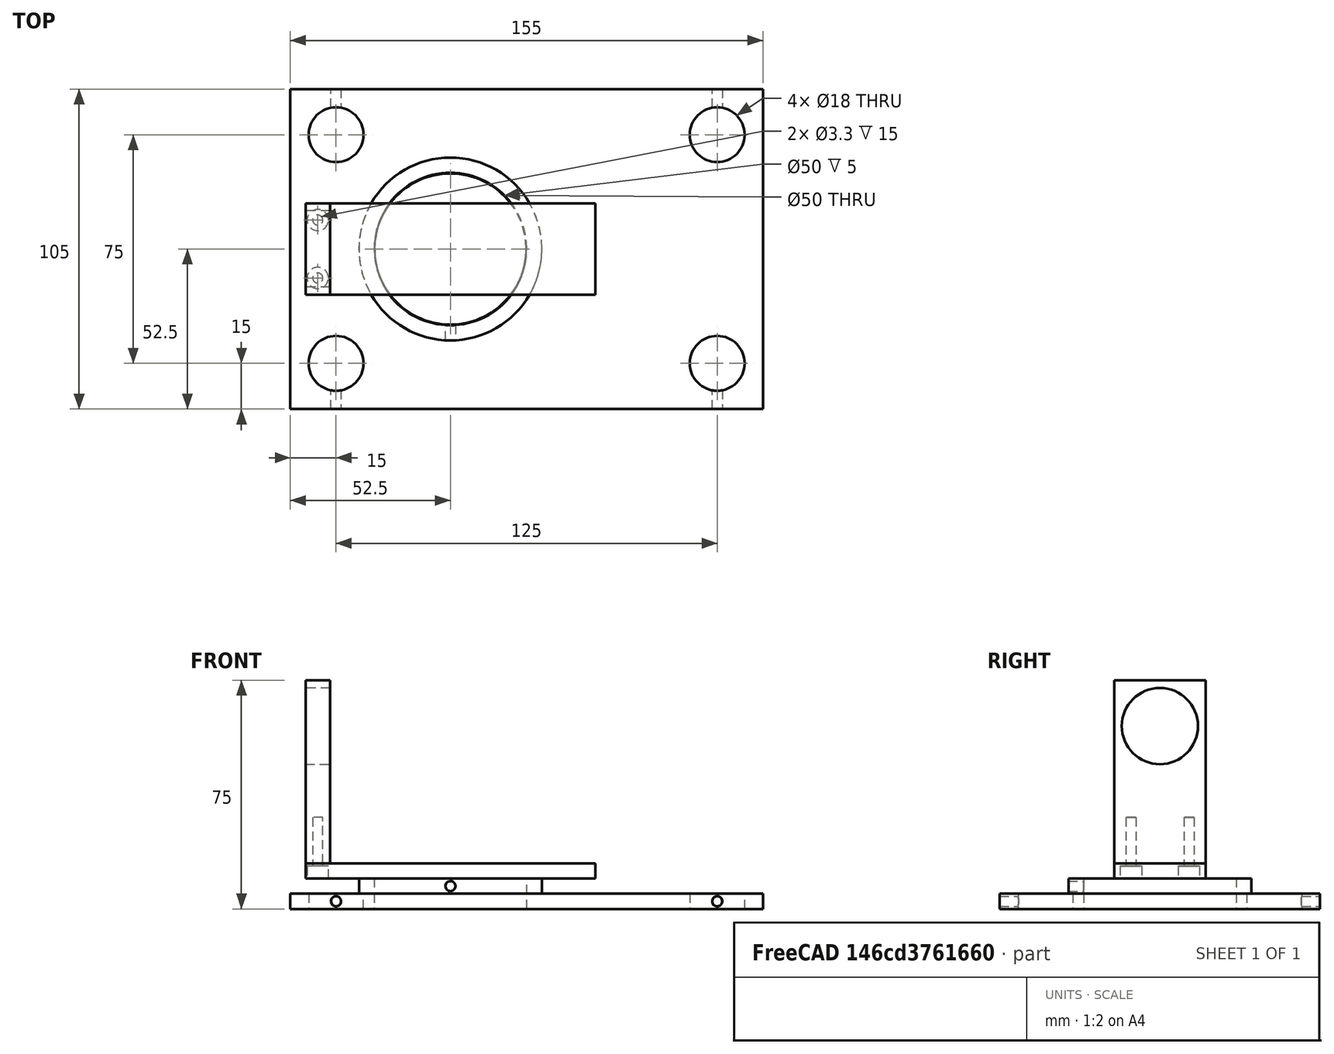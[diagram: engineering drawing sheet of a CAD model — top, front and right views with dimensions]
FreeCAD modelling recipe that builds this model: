
FCSTD DOCUMENT  (FreeCAD 0.21R33675 (Git))
Label: CameraObjectiveMount01
License: All rights reserved
LicenseURL: http://en.wikipedia.org/wiki/All_rights_reserved
objects: Part::Cylinder×20, Part::Cut×8, Part::Compound×4, Part::MultiFuse×4, Part::Box×3, Part::Feature×3
note: 42 computed .brp shape members not serialized (recipe doc carries the construction recipe); baked Part::Feature solids carry a one-line shape summary decoded from their .brp

FEATURE [Part::Box] Box  label="Würfel"
  AttacherType = Attacher::AttachEngine3D
  Height = 5
  Length = 155
  Placement = pos=(-5,-5,0) rot=(0,0,1;0rad)
  Width = 105
FEATURE [Part::Cylinder] Cylinder  label="Zylinder"
  Angle = 360
  AttacherType = Attacher::AttachEngine3D
  FirstAngle = 0
  Height = 100
  Placement = pos=(10,10,-10) rot=(0,0,1;0rad)
  Radius = 9
  SecondAngle = 0
FEATURE [Part::Cylinder] Cylinder001  label="Zylinder001"
  Angle = 360
  AttacherType = Attacher::AttachEngine3D
  FirstAngle = 0
  Height = 100
  Placement = pos=(135,85,-10) rot=(0,0,1;0rad)
  Radius = 9
  SecondAngle = 0
FEATURE [Part::Cylinder] Cylinder002  label="Zylinder002"
  Angle = 360
  AttacherType = Attacher::AttachEngine3D
  FirstAngle = 0
  Height = 100
  Placement = pos=(10,85,-10) rot=(0,0,1;0rad)
  Radius = 9
  SecondAngle = 0
FEATURE [Part::Cylinder] Cylinder003  label="Zylinder003"
  Angle = 360
  AttacherType = Attacher::AttachEngine3D
  FirstAngle = 0
  Height = 100
  Placement = pos=(135,10,-10) rot=(0,0,1;0rad)
  Radius = 9
  SecondAngle = 0
FEATURE [Part::Compound] Compound  label="Posts1"
  Links = -> [Cylinder,Cylinder001,Cylinder002,Cylinder003]
FEATURE [Part::Cut] Cut
  Base = -> Box
  Tool = -> Compound
FEATURE [Part::Cylinder] Cylinder004  label="Zylinder004"
  Angle = 360
  AttacherType = Attacher::AttachEngine3D
  FirstAngle = 0
  Height = 10
  Placement = pos=(10,5,2.5) rot=(1,0,0;1.5708rad)
  Radius = 1.65
  SecondAngle = 0
FEATURE [Part::Cylinder] Cylinder005  label="Zylinder005"
  Angle = 360
  AttacherType = Attacher::AttachEngine3D
  FirstAngle = 0
  Height = 10
  Placement = pos=(10,100,2.5) rot=(1,0,0;1.5708rad)
  Radius = 1.65
  SecondAngle = 0
FEATURE [Part::Cylinder] Cylinder006  label="Zylinder006"
  Angle = 360
  AttacherType = Attacher::AttachEngine3D
  FirstAngle = 0
  Height = 10
  Placement = pos=(135,5,2.5) rot=(1,0,0;1.5708rad)
  Radius = 1.65
  SecondAngle = 0
FEATURE [Part::Cylinder] Cylinder007  label="Zylinder007"
  Angle = 360
  AttacherType = Attacher::AttachEngine3D
  FirstAngle = 0
  Height = 10
  Placement = pos=(135,100,2.5) rot=(1,0,0;1.5708rad)
  Radius = 1.65
  SecondAngle = 0
FEATURE [Part::Compound] Compound001
  Links = -> [Cylinder007,Cylinder004,Cylinder005,Cylinder006]
FEATURE [Part::Cut] Cut001
  Base = -> Cut
  Tool = -> Compound001
FEATURE [Part::Cylinder] Cylinder008  label="Zylinder008"
  Angle = 360
  AttacherType = Attacher::AttachEngine3D
  FirstAngle = 0
  Height = 5
  Placement = pos=(47.5,47.5,5) rot=(0,0,1;0rad)
  Radius = 30
  SecondAngle = 0
FEATURE [Part::Cylinder] Cylinder009  label="Zylinder009"
  Angle = 360
  AttacherType = Attacher::AttachEngine3D
  FirstAngle = 0
  Height = 10
  Placement = pos=(47.5,47.5,0) rot=(0,0,1;0rad)
  Radius = 25
  SecondAngle = 0
FEATURE [Part::Cut] Cut002
  Base = -> Cylinder008
  Tool = -> Cylinder009
FEATURE [Part::Cylinder] Cylinder010  label="Zylinder010"
  Angle = 360
  AttacherType = Attacher::AttachEngine3D
  FirstAngle = 0
  Height = 10
  Placement = pos=(47.5,47.5,0) rot=(0,0,1;0rad)
  Radius = 24.8
  SecondAngle = 0
FEATURE [Part::Box] Box001  label="Würfel001"
  AttacherType = Attacher::AttachEngine3D
  Height = 5
  Length = 95
  Placement = pos=(0,32.5,10) rot=(0,0,1;0rad)
  Width = 30
FEATURE [Part::Box] Box002  label="Würfel002"
  AttacherType = Attacher::AttachEngine3D
  Height = 60
  Length = 8
  Placement = pos=(0,32.5,15) rot=(0,0,1;0rad)
  Width = 30
FEATURE [Part::Cylinder] Cylinder011  label="Zylinder011"
  Angle = 360
  AttacherType = Attacher::AttachEngine3D
  FirstAngle = 0
  Height = 10
  Placement = pos=(0,47.5,60) rot=(0,1,0;1.5708rad)
  Radius = 12.5
  SecondAngle = 0
FEATURE [Part::Cut] Cut003
  Base = -> Box002
  Tool = -> Cylinder011
FEATURE [Part::Cylinder] Cylinder012  label="Zylinder012"
  Angle = 360
  AttacherType = Attacher::AttachEngine3D
  FirstAngle = 0
  Height = 10
  Placement = pos=(47.5,47.5,0) rot=(0,0,1;0rad)
  Radius = 25
  SecondAngle = 0
FEATURE [Part::Cut] Cut004
  Base = -> Cut001
  Tool = -> Cylinder012
FEATURE [Part::Cylinder] Cylinder013  label="Zylinder013"
  Angle = 360
  AttacherType = Attacher::AttachEngine3D
  FirstAngle = 0
  Height = 10
  Placement = pos=(47.5,25,7.5) rot=(1,0,0;1.5708rad)
  Radius = 1.65
  SecondAngle = 0
FEATURE [Part::MultiFuse] Fusion
  Shapes = -> [Cut002,Cut004]
FEATURE [Part::Cut] Cut005  label="Plate"
  Base = -> Fusion
  Tool = -> Cylinder013
FEATURE [Part::MultiFuse] Fusion001
  Shapes = -> [Cylinder010,Box001]
FEATURE [Part::Cylinder] Cylinder014  label="Zylinder014"
  Angle = 360
  AttacherType = Attacher::AttachEngine3D
  FirstAngle = 0
  Height = 20
  Radius = 1.65
  SecondAngle = 0
FEATURE [Part::Cylinder] Cylinder015  label="Zylinder015"
  Angle = 360
  AttacherType = Attacher::AttachEngine3D
  FirstAngle = 0
  Height = 20
  Radius = 1.65
  SecondAngle = 0
FEATURE [Part::Cylinder] Cylinder016  label="Zylinder016"
  Angle = 360
  AttacherType = Attacher::AttachEngine3D
  FirstAngle = 0
  Height = 4
  Radius = 3.5
  SecondAngle = 0
FEATURE [Part::Cylinder] Cylinder017  label="Zylinder017"
  Angle = 360
  AttacherType = Attacher::AttachEngine3D
  FirstAngle = 0
  Height = 4
  Radius = 3.5
  SecondAngle = 0
FEATURE [Part::MultiFuse] Fusion002  label="Screw01"
  Placement = pos=(4,38,10) rot=(0,0,1;0rad)
  Shapes = -> [Cylinder014,Cylinder016]
FEATURE [Part::MultiFuse] Fusion003  label="Screw02"
  Placement = pos=(4,57,10) rot=(0,0,1;0rad)
  Shapes = -> [Cylinder015,Cylinder017]
FEATURE [Part::Compound] Compound002
  Links = -> [Fusion002,Fusion003]
FEATURE [Part::Cut] Cut006  label="RotatingTable"
  Base = -> Fusion001
  Tool = -> Compound002
FEATURE [Part::Cylinder] Cylinder018  label="Zylinder018"
  Angle = 360
  AttacherType = Attacher::AttachEngine3D
  FirstAngle = 0
  Height = 20
  Placement = pos=(4,38,10) rot=(0,0,1;0rad)
  Radius = 1.65
  SecondAngle = 0
FEATURE [Part::Cylinder] Cylinder019  label="Zylinder019"
  Angle = 360
  AttacherType = Attacher::AttachEngine3D
  FirstAngle = 0
  Height = 20
  Placement = pos=(4,57,10) rot=(0,0,1;0rad)
  Radius = 1.65
  SecondAngle = 0
FEATURE [Part::Compound] Compound003
  Links = -> [Cylinder019,Cylinder018]
FEATURE [Part::Cut] Cut007  label="CameraHolder"
  Base = -> Cut003
  Tool = -> Compound003
FEATURE [Part::Feature] Cut005_solid  label="Plate (Solid)"
  shape: bbox 155 x 105 x 10 mm, 19 faces (baked)
FEATURE [Part::Feature] Cut006_solid  label="RotatingTable (Solid)"
  shape: bbox 95 x 49.6 x 15 mm, 17 faces (baked)
FEATURE [Part::Feature] Cut007_solid  label="CameraHolder (Solid)"
  shape: bbox 8 x 30 x 60 mm, 11 faces (baked)
